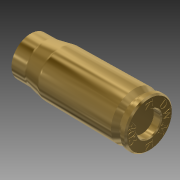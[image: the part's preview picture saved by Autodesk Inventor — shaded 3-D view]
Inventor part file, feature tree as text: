
AUTODESK INVENTOR PART (.ipt)
format: ipt  version: 2011 SP1 (Build 150282100, 282)  size: 751,616 bytes
history: native  units: mm
features: sketch x6, extrude x5, other x1, revolve x1, shell x1, fillet x1
ambient origin geometry x8: Origin, YZ Plane, XZ Plane, XY Plane, X Axis, Y Axis, Z Axis, Center Point
feature tree (15):
  other  "Твердое тело1"
  revolve  "Вращение1"
  extrude  "Выдавливание1"  TaperAngle=90.0deg  [1 undecoded]
  extrude  "Выдавливание2"  Depth=18.601302mm
  shell  "Оболочка1"  Thickness=45.0mm
  extrude  "Выдавливание3"  Depth=1.25mm TaperAngle=0.0deg
  extrude  "Выдавливание4"  Depth=0.3mm
  extrude  "Выдавливание5"  Depth=0.3mm
  fillet  "Сопряжение2"  Radius=0.3mm
  sketch  "Эскиз1"
  sketch  "Эскиз2"
  sketch  "Эскиз3"
  sketch  "Эскиз4"
  sketch  "Эскиз5"
  sketch  "Эскиз6"
note: 1 required parameter value undecoded (feature->parameter linkage not recoverable at this tier; creation-order binding heuristic only, values carry confidence <= 0.55)
